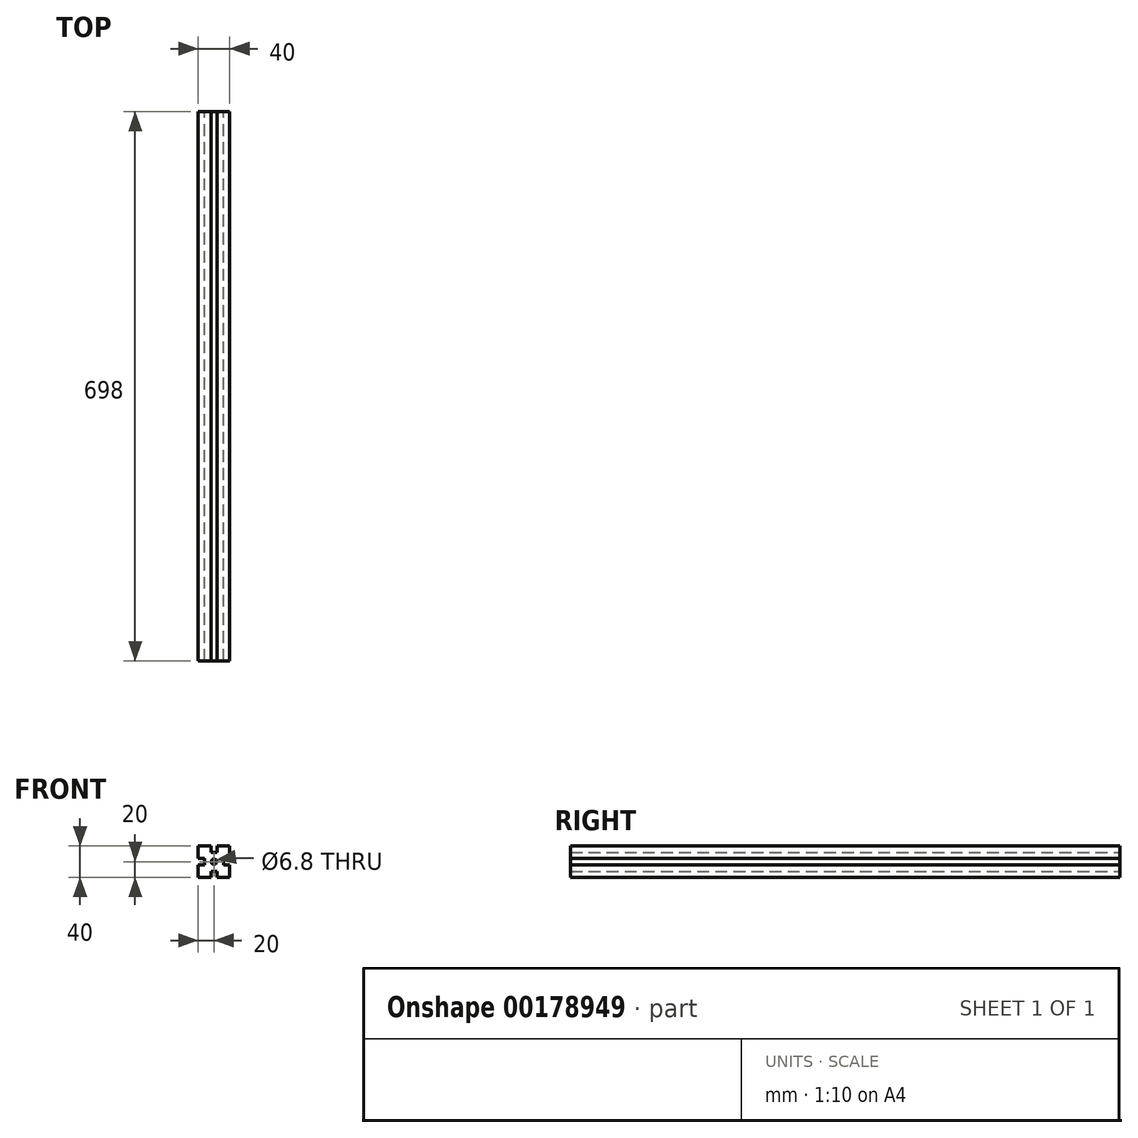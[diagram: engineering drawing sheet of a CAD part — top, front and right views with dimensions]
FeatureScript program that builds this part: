
annotation { "Feature Type Name" : "Feature", "Feature Type Description" : "" }
export const myFeature = defineFeature(function(context is Context, id is Id, definition is map)
    precondition{}
    {
        {
            var Q0;
            Q0=qCreatedBy(makeId("Front.planeOp"),FACE);
            var sketch = newSketch(context, id + "F0", { "sketchPlane" : qUnion([Q0])});
            skLineSegment(sketch, "E0.bottom", {"start": v(20, 20) * mm, "end": v(4, 20) * mm});
            skLineSegment(sketch, "E0.top", {"start": v(20, -20) * mm, "end": v(4.03, -20) * mm});
            skLineSegment(sketch, "E0.left", {"start": v(20, 20) * mm, "end": v(20, 3.99) * mm});
            skLineSegment(sketch, "E0.right", {"start": v(-20, 20) * mm, "end": v(-20, 4) * mm});
            skPoint(sketch, "E0.middle", {"position": v(0, 0) * mm});
            skCircle(sketch, "E1", {"center": v(0, 0) * mm, "radius": 3.4 * mm});
            skLineSegment(sketch, "E2.bottom", {"start": v(4, 12) * mm, "end": v(-4, 12) * mm});
            skLineSegment(sketch, "E2.left", {"start": v(4, 12) * mm, "end": v(4, 20) * mm});
            skLineSegment(sketch, "E2.right", {"start": v(-4, 12) * mm, "end": v(-4, 20) * mm});
            skPoint(sketch, "E2.middle", {"position": v(0, 20) * mm});
            skLineSegment(sketch, "E3.top", {"start": v(4.03, -12.02) * mm, "end": v(-3.97, -12.02) * mm});
            skLineSegment(sketch, "E3.left", {"start": v(4.03, -20) * mm, "end": v(4.03, -12.02) * mm});
            skLineSegment(sketch, "E3.right", {"start": v(-3.97, -20) * mm, "end": v(-3.97, -12.02) * mm});
            skLineSegment(sketch, "E4.bottom", {"start": v(-12, -4) * mm, "end": v(-20, -4) * mm});
            skLineSegment(sketch, "E4.top", {"start": v(-12, 4) * mm, "end": v(-20, 4) * mm});
            skLineSegment(sketch, "E4.left", {"start": v(-12, -4) * mm, "end": v(-12, 4) * mm});
            skPoint(sketch, "E4.middle", {"position": v(-20, 0) * mm});
            skLineSegment(sketch, "E5.bottom", {"start": v(20, -4.01) * mm, "end": v(12.01, -4.01) * mm});
            skLineSegment(sketch, "E5.top", {"start": v(20, 3.99) * mm, "end": v(12.01, 3.99) * mm});
            skLineSegment(sketch, "E5.right", {"start": v(12.01, -4.01) * mm, "end": v(12.01, 3.99) * mm});
            skLineSegment(sketch, "E6.trimOffspring", {"start": v(-20, -4) * mm, "end": v(-20, -20) * mm});
            skPoint(sketch, "E4.right.end.orphan", {"position": v(-28, 4) * mm});
            skPoint(sketch, "E4.right.start.orphan", {"position": v(-28, -4) * mm});
            skPoint(sketch, "E7.orphan", {"position": v(-4, 28) * mm});
            skPoint(sketch, "E8.orphan", {"position": v(4, 28) * mm});
            skLineSegment(sketch, "E9.trimOffspring", {"start": v(-4, 20) * mm, "end": v(-20, 20) * mm});
            skLineSegment(sketch, "E10.trimOffspring", {"start": v(20, -4.01) * mm, "end": v(20, -20) * mm});
            skLineSegment(sketch, "E11.trimOffspring", {"start": v(-3.97, -20) * mm, "end": v(-20, -20) * mm});
            skSolve(sketch);
        }
        {
            var Q0;
            Q0=makeQuery(id+"F0.imprint","IMPRINT",FACE,{"disambiguationData":[TD([[makeQuery(id+"F0.imprint","IMPRINT",EDGE,{"derivedFrom":sQuery(id+"F0.wireOp",EDGE,"E0.bottom")}),1.0]])]});
            extrude(context, id + "F1", {"entities" : qUnion([Q0]), "depth" : 698 * mm});
        }
    });
